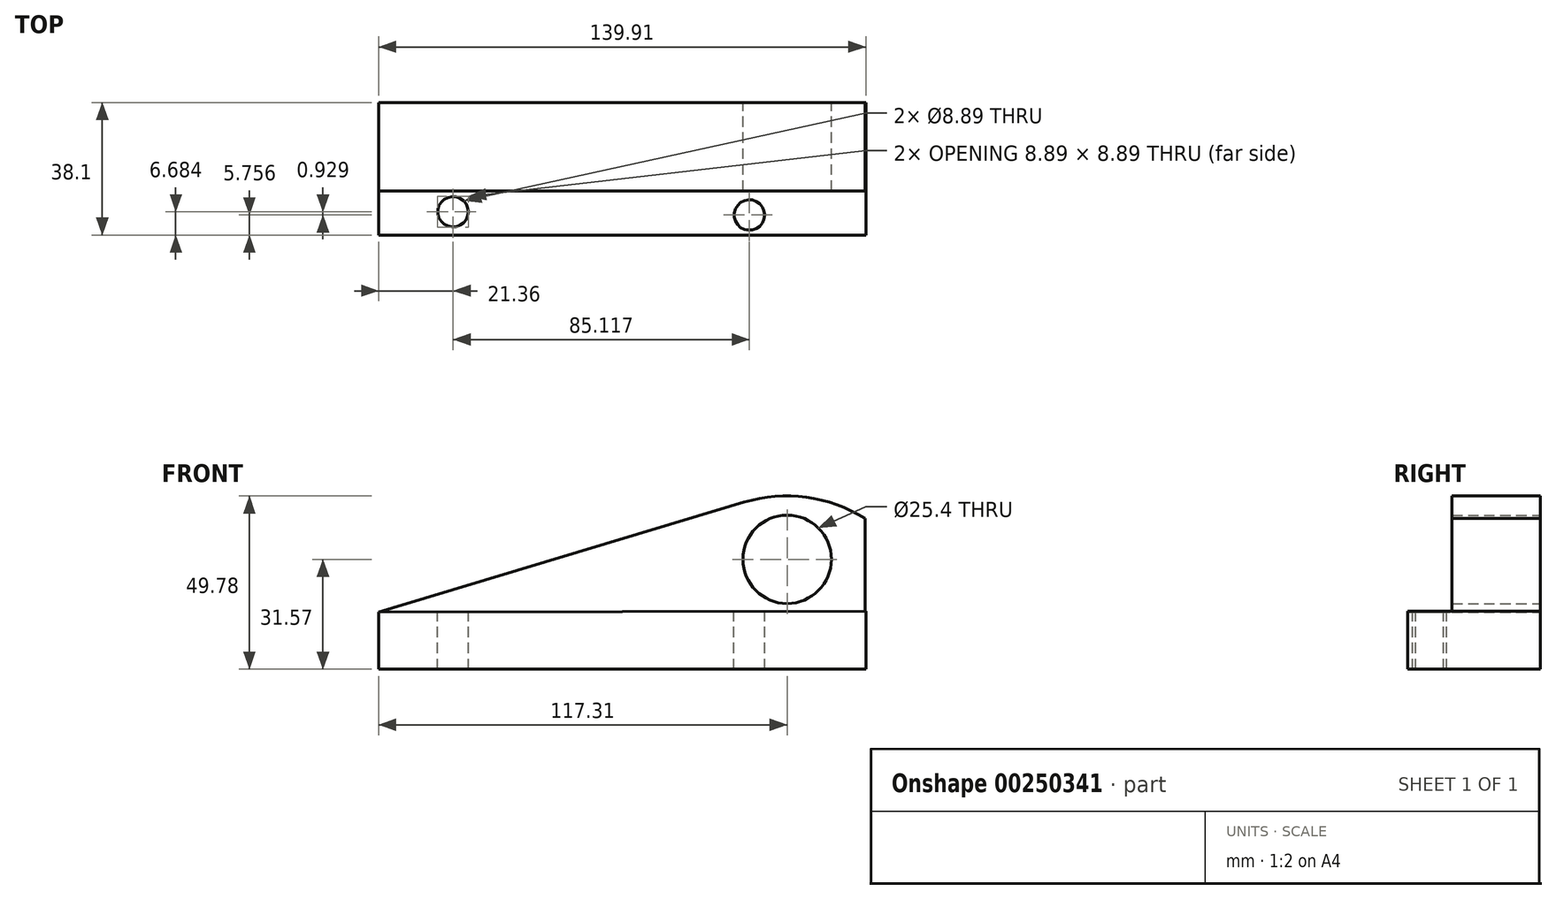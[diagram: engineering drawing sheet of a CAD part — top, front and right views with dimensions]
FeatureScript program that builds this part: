
annotation { "Feature Type Name" : "Feature", "Feature Type Description" : "" }
export const myFeature = defineFeature(function(context is Context, id is Id, definition is map)
    precondition{}
    {
        {
            var Q0;
            Q0=qCreatedBy(makeId("Front.planeOp"),FACE);
            var sketch = newSketch(context, id + "F0", { "sketchPlane" : qUnion([Q0])});
            skLineSegment(sketch, "E0", {"start": v(-72.74, -37.92) * mm, "end": v(66.96, -37.92) * mm});
            skPoint(sketch, "E1.end.orphan", {"position": v(66.96, -10.99) * mm});
            skPoint(sketch, "E2.start.orphan", {"position": v(66.96, 0) * mm});
            skPoint(sketch, "E3.end.orphan", {"position": v(32.19, 0) * mm});
            skLineSegment(sketch, "E4", {"start": v(66.96, -10.99) * mm, "end": v(66.96, -37.92) * mm});
            skLineSegment(sketch, "E5", {"start": v(-72.74, -37.92) * mm, "end": v(32.19, -6.35) * mm});
            skArc(sketch, "E6", {"start": v(66.96, -10.99) * mm, "mid": v(50.08, -4.92) * mm, "end": v(32.19, -6.35) * mm});
            skSolve(sketch);
        }
        {
            var Q0;
            Q0=qCreatedBy(makeId("Front.planeOp"),FACE);
            var sketch = newSketch(context, id + "F1", { "sketchPlane" : qUnion([Q0])});
            skLineSegment(sketch, "E7", {"start": v(67.17, -37.6) * mm, "end": v(67.17, -54.32) * mm});
            skLineSegment(sketch, "E8", {"start": v(67.17, -54.32) * mm, "end": v(-72.74, -54.32) * mm});
            skLineSegment(sketch, "E9", {"start": v(-72.74, -54.32) * mm, "end": v(-72.74, -37.92) * mm});
            skLineSegment(sketch, "E10", {"start": v(-72.74, -37.92) * mm, "end": v(67.17, -37.6) * mm});
            skSolve(sketch);
        }
        {
            var Q0;
            Q0=makeQuery(id+"F0.imprint","IMPRINT",FACE,{"disambiguationData":[TD([[makeQuery(id+"F0.imprint","IMPRINT",EDGE,{"derivedFrom":sQuery(id+"F0.wireOp",EDGE,"E0")}),1.0]])]});
            extrude(context, id + "F2", {"entities" : qUnion([Q0]), "depth" : 25.4 * mm});
        }
        {
            var Q0;
            Q0=makeQuery(id+"F1.imprint","IMPRINT",FACE,{"disambiguationData":[TD([[makeQuery(id+"F1.imprint","IMPRINT",EDGE,{"derivedFrom":sQuery(id+"F1.wireOp",EDGE,"E7")}),-1.0]])]});
            extrude(context, id + "F3", {"entities" : qUnion([Q0]), "operationType" : NewBodyOperationType.ADD, "depth" : 38.1 * mm});
        }
        {
            var Q0;
            Q0=qCreatedBy(makeId("Front.planeOp"),FACE);
            var sketch = newSketch(context, id + "F4", { "sketchPlane" : qUnion([Q0])});
            skLineSegment(sketch, "E11", {"start": v(44.57, -22.75) * mm, "end": v(28.79, -22.75) * mm});
            skSolve(sketch);
        }
        {
            var Q0;
            Q0=sQuery(id+"F4.wireOp",VERTEX,"E11.start");
            var Q1;
            Q1=makeQuery(id+"F2.opExtrude","SWEPT_BODY",BODY,{"disambiguationData":[OSD([sQuery(id+"F0.wireOp",EDGE,"E0"),sQuery(id+"F0.wireOp",EDGE,"E4"),sQuery(id+"F0.wireOp",EDGE,"E5"),sQuery(id+"F0.wireOp",EDGE,"E6")])]});
            hole(context, id + "F5", {"style" : HoleStyle.SIMPLE, "endStyle" : HoleEndStyle.THROUGH, "oppositeDirection" : true, "holeDiameter" : 25.4 * mm, "tappedDepth" : 12.7 * mm, "tapClearance" : 3, "locations" : qUnion([Q0]), "scope" : qUnion([Q1])});
        }
        {
            var Q0;
            Q0=qCreatedBy(makeId("Top.planeOp"),FACE);
            var sketch = newSketch(context, id + "F6", { "sketchPlane" : qUnion([Q0])});
            skLineSegment(sketch, "E12", {"start": v(-51.38, -31.42) * mm, "end": v(-65.62, -31.42) * mm});
            skSolve(sketch);
        }
        {
            var Q0;
            Q0=sQuery(id+"F6.wireOp",VERTEX,"E12.start");
            var Q1;
            Q1=makeQuery(id+"F2.opExtrude","SWEPT_BODY",BODY,{"disambiguationData":[OSD([sQuery(id+"F0.wireOp",EDGE,"E0"),sQuery(id+"F0.wireOp",EDGE,"E4"),sQuery(id+"F0.wireOp",EDGE,"E5"),sQuery(id+"F0.wireOp",EDGE,"E6")])]});
            hole(context, id + "F7", {"style" : HoleStyle.SIMPLE, "endStyle" : HoleEndStyle.THROUGH, "holeDiameter" : 8.9 * mm, "tappedDepth" : 12.7 * mm, "tapClearance" : 3, "locations" : qUnion([Q0]), "scope" : qUnion([Q1])});
        }
        {
            var Q0;
            Q0=qCreatedBy(makeId("Top.planeOp"),FACE);
            var sketch = newSketch(context, id + "F8", { "sketchPlane" : qUnion([Q0])});
            skLineSegment(sketch, "E13", {"start": v(33.74, -32.34) * mm, "end": v(21.98, -32.34) * mm});
            skSolve(sketch);
        }
        {
            var Q0;
            Q0=sQuery(id+"F8.wireOp",VERTEX,"E13.start");
            var Q1;
            Q1=makeQuery(id+"F2.opExtrude","SWEPT_BODY",BODY,{"disambiguationData":[OSD([sQuery(id+"F0.wireOp",EDGE,"E0"),sQuery(id+"F0.wireOp",EDGE,"E4"),sQuery(id+"F0.wireOp",EDGE,"E5"),sQuery(id+"F0.wireOp",EDGE,"E6")])]});
            hole(context, id + "F9", {"style" : HoleStyle.SIMPLE, "endStyle" : HoleEndStyle.THROUGH, "holeDiameter" : 8.9 * mm, "tappedDepth" : 12.7 * mm, "tapClearance" : 3, "locations" : qUnion([Q0]), "scope" : qUnion([Q1])});
        }
    });
